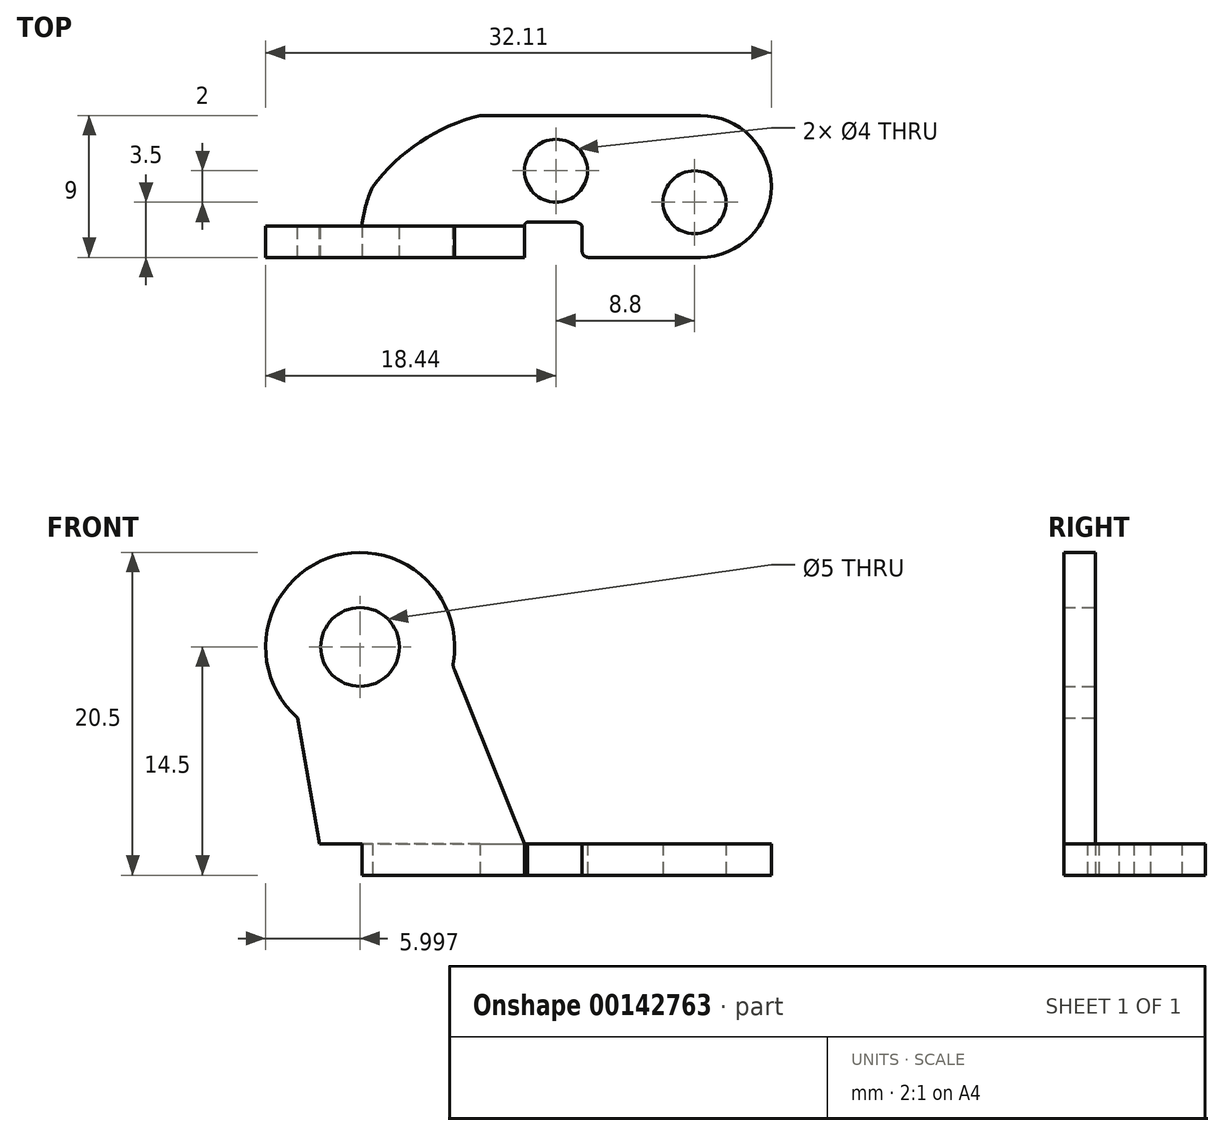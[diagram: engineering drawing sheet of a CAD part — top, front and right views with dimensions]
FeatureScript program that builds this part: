
annotation { "Feature Type Name" : "Feature", "Feature Type Description" : "" }
export const myFeature = defineFeature(function(context is Context, id is Id, definition is map)
    precondition{}
    {
        {
            var Q0;
            Q0=qCreatedBy(makeId("Front.planeOp"),FACE);
            var sketch = newSketch(context, id + "F0", { "sketchPlane" : qUnion([Q0])});
            skLineSegment(sketch, "E0", {"start": v(0, 0) * mm, "end": v(0, 2) * mm});
            skLineSegment(sketch, "E1", {"start": v(0, 2) * mm, "end": v(26, 2) * mm});
            skLineSegment(sketch, "E2", {"start": v(26, 2) * mm, "end": v(26, 0) * mm});
            skLineSegment(sketch, "E3", {"start": v(26, 0) * mm, "end": v(0, 0) * mm});
            skArc(sketch, "E4", {"start": v(8.48, 13.56) * mm, "mid": v(0.52, 20.15) * mm, "end": v(-1.41, 10) * mm});
            skLineSegment(sketch, "E5", {"start": v(0, 2) * mm, "end": v(-1.41, 10) * mm});
            skLineSegment(sketch, "E6", {"start": v(8.54, 13.03) * mm, "end": v(13, 2) * mm});
            skCircle(sketch, "E7", {"center": v(2.56, 14.5) * mm, "radius": 2.5 * mm});
            skPoint(sketch, "E8.visualSharp", {"position": v(8.44, 13.3) * mm});
            skArc(sketch, "E8.filletArc", {"start": v(8.48, 13.56) * mm, "mid": v(8.48, 13.3) * mm, "end": v(8.54, 13.03) * mm});
            skSolve(sketch);
        }
        {
            var Q0;
            Q0=makeQuery(id+"F0.imprint","IMPRINT",FACE,{"disambiguationData":[TD([[makeQuery(id+"F0.imprint","IMPRINT",EDGE,{"derivedFrom":sQuery(id+"F0.wireOp",EDGE,"E4")}),1.0]])]});
            extrude(context, id + "F1", {"entities" : qUnion([Q0]), "depth" : 2 * mm});
        }
        {
            var Q0;
            Q0=qCreatedBy(makeId("Top.planeOp"),FACE);
            var sketch = newSketch(context, id + "F2", { "sketchPlane" : qUnion([Q0])});
            skLineSegment(sketch, "E9.0", {"start": v(0, -2) * mm, "end": v(0, 0) * mm, "construction": true});
            skLineSegment(sketch, "E10.0", {"start": v(0, -2) * mm, "end": v(13, -2) * mm, "construction": true});
            skLineSegment(sketch, "E11.0", {"start": v(13, -2) * mm, "end": v(13, 0) * mm, "construction": true});
            skCircle(sketch, "E12", {"center": v(23.8, 1.5) * mm, "radius": 2 * mm});
            skCircle(sketch, "E13", {"center": v(15, 3.5) * mm, "radius": 2 * mm});
            skLineSegment(sketch, "E14", {"start": v(10.17, 7) * mm, "end": v(24.17, 7) * mm});
            skLineSegment(sketch, "E15", {"start": v(17.05, -2) * mm, "end": v(24.17, -2) * mm});
            skPoint(sketch, "E16.center.orphan", {"position": v(27.8, 2.5) * mm});
            skPoint(sketch, "E17.start.orphan", {"position": v(27.8, -2) * mm});
            skArc(sketch, "E18", {"start": v(24.17, -2) * mm, "mid": v(28.67, 2.5) * mm, "end": v(24.17, 7) * mm});
            skLineSegment(sketch, "E19", {"start": v(28.67, 2.5) * mm, "end": v(28.67, 6.18) * mm, "construction": true});
            skLineSegment(sketch, "E20", {"start": v(28.67, 6.18) * mm, "end": v(28.12, 6.18) * mm, "construction": true});
            skLineSegment(sketch, "E21", {"start": v(13, 0) * mm, "end": v(2.67, 0) * mm});
            skArc(sketch, "E22", {"start": v(3.36, 2.47) * mm, "mid": v(2.91, 1.26) * mm, "end": v(2.67, 0) * mm});
            skArc(sketch, "E23", {"start": v(10.17, 7) * mm, "mid": v(6.36, 5.33) * mm, "end": v(3.36, 2.47) * mm});
            skLineSegment(sketch, "E24", {"start": v(2.67, 0) * mm, "end": v(2.67, -2) * mm});
            skLineSegment(sketch, "E25", {"start": v(2.67, -2) * mm, "end": v(13, -2) * mm});
            skArc(sketch, "E26", {"start": v(13.2, 0.24) * mm, "mid": v(13.06, 0.16) * mm, "end": v(13, 0) * mm});
            skLineSegment(sketch, "E27", {"start": v(16.66, -1.62) * mm, "end": v(16.66, 0) * mm});
            skArc(sketch, "E28", {"start": v(16.66, -1.62) * mm, "mid": v(16.77, -1.89) * mm, "end": v(17.05, -2) * mm});
            skLineSegment(sketch, "E29", {"start": v(13.2, 0.24) * mm, "end": v(16.2, 0.24) * mm});
            skArc(sketch, "E30", {"start": v(16.66, 0) * mm, "mid": v(16.46, 0.18) * mm, "end": v(16.2, 0.24) * mm});
            skLineSegment(sketch, "E31", {"start": v(13, -2) * mm, "end": v(13, 0) * mm});
            skSolve(sketch);
        }
        {
            var Q0;
            Q0 = qSketchRegion(id + "F2", true);
            extrude(context, id + "F3", {"entities" : qUnion([Q0]), "operationType" : NewBodyOperationType.ADD, "depth" : 2 * mm});
        }
    });
